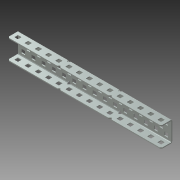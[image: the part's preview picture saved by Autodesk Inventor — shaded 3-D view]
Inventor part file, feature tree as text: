
AUTODESK INVENTOR PART (.ipt)
format: ipt  version: 2015 (Build 190159000, 159)  size: 1,670,656 bytes
history: native  units: mm (DEFAULTED — no unit token found)
features: other x74, extrude x74, pattern_linear x3, sketch x2, imported_body x1, plane x1, mirror x1
ambient origin geometry x8: Origin, YZ Plane, XZ Plane, XY Plane, X Axis, Y Axis, Z Axis, Center Point
bodies: Solid1 (feature_tree)
feature tree (156):
  imported_body  "Base1"
  sketch  "Sketch1"  dims[d1=1.1684mm]
  pattern_linear  "Rectangular Pattern1"  Spacing1=1.1684mm  [1 undecoded]
  pattern_linear  "Rectangular Pattern2"  Spacing1=0.0mm  [1 undecoded]
  pattern_linear  "Rectangular Pattern3"  Count1=15  [1 undecoded]
  plane  "Work Plane1"
  mirror  "Mirror1"
  other  "Srf1"
  other  "Srf2"
  other  "Srf3"
  other  "Srf4"
  other  "Srf5"
  other  "Srf6"
  other  "Srf17"
  other  "Srf18"
  other  "Srf19"
  other  "Srf20"
  other  "Srf21"
  other  "Srf32"
  other  "Srf33"
  other  "Srf34"
  other  "Srf7"
  other  "Srf8"
  other  "Srf9"
  other  "Srf10"
  other  "Srf11"
  other  "Srf12"
  other  "Srf13"
  other  "Srf14"
  other  "Srf15"
  other  "Srf16"
  other  "Srf22"
  other  "Srf23"
  other  "Srf24"
  other  "Srf25"
  other  "Srf26"
  other  "Srf27"
  other  "Srf28"
  other  "Srf29"
  other  "Srf30"
  other  "Srf31"
  other  "Srf35"
  other  "Srf36"
  other  "Srf37"
  other  "Srf38"
  other  "Srf39"
  other  "Srf40"
  other  "Srf41"
  other  "Srf42"
  other  "Srf43"
  other  "Srf44"
  sketch  "Sketch2"  dims[d2=0.0mm d3=1.1684mm d4=0.0mm d5=150.0mm d7=12.7mm d8=20.0mm d10=12.7mm d11=140.0mm d13=12.7mm d14=1.1684mm d15=0.0mm d16=150.0mm d18=12.7mm d19=0.0mm d20=0.0mm d21=0.0mm d22=0.0mm d23=0.0mm d24=0.0mm d25=0.0mm d26=0.0mm d27=0.0mm d28=0.0mm d29=0.0mm d30=0.0mm d31=0.0mm d32=0.0mm d33=0.0mm d34=0.0mm d35=0.0mm d36=0.0mm d37=0.0mm d38=0.0mm d39=0.0mm d40=0.0mm d41=0.0mm d42=0.0mm d43=0.0mm d44=0.0mm d45=0.0mm d46=0.0mm d47=0.0mm d48=0.0mm d49=0.0mm d50=0.0mm d51=0.0mm d52=0.0mm d53=0.0mm d54=0.0mm d55=0.0mm d56=0.0mm d57=0.0mm d58=0.0mm d59=0.0mm d60=0.0mm d61=0.0mm d62=0.0mm d63=0.0mm d64=0.0mm d65=0.0mm d66=0.0mm d67=0.0mm d68=0.0mm d69=0.0mm d70=0.0mm d71=0.0mm d72=0.0mm d73=0.0mm d74=0.0mm d75=0.0mm d76=0.0mm d77=0.0mm d78=0.0mm d79=0.0mm d80=0.0mm d81=0.0mm d82=0.0mm d83=0.0mm d84=0.0mm d85=0.0mm d86=0.0mm d87=0.0mm d88=0.0mm d89=0.0mm d90=0.0mm d91=0.0mm d92=0.0mm d93=0.0mm d94=0.0mm d95=0.0mm d96=0.0mm d97=0.0mm d98=0.0mm d99=0.0mm d100=0.0mm d101=0.0mm d102=0.0mm d103=0.0mm d104=0.0mm d105=0.0mm d106=0.0mm d107=0.0mm d108=0.0mm d109=0.0mm d110=0.0mm d111=0.0mm d112=0.0mm d113=0.0mm d114=0.0mm d115=0.0mm d116=0.0mm d117=0.0mm d118=0.0mm d119=0.0mm d120=0.0mm d121=0.0mm d122=0.0mm d123=0.0mm d124=0.0mm d125=0.0mm d126=0.0mm d127=0.0mm d128=0.0mm d129=0.0mm d130=0.0mm d131=0.0mm d132=0.0mm d133=0.0mm d134=0.0mm d135=0.0mm d136=0.0mm d137=0.0mm d138=0.0mm d139=0.0mm d140=0.0mm d141=0.0mm d142=0.0mm d143=0.0mm d144=0.0mm d145=0.0mm d146=0.0mm d147=0.0mm d148=0.0mm d149=0.0mm d150=0.0mm d151=0.0mm d152=0.0mm d153=0.0mm d154=0.0mm d155=0.0mm d156=0.0mm d157=0.0mm d158=0.0mm d159=0.0mm d160=0.0mm d161=0.0mm d162=0.0mm d163=0.0mm d164=0.0mm d165=0.0mm d166=0.0mm]
  other  "Srf45"
  other  "Srf46"
  other  "Srf47"
  other  "Srf48"
  other  "Srf49"
  other  "Srf50"
  other  "Srf51"
  other  "Srf52"
  other  "Srf53"
  other  "Srf54"
  other  "Srf55"
  other  "Srf56"
  other  "Srf57"
  other  "Srf58"
  other  "Srf59"
  other  "Srf60"
  other  "Srf61"
  other  "Srf62"
  other  "Srf63"
  other  "Srf64"
  other  "Srf65"
  other  "Srf66"
  other  "Srf67"
  other  "Srf68"
  other  "Srf69"
  other  "Srf70"
  other  "Srf71"
  other  "Srf72"
  other  "Srf73"
  other  "Srf74"
  extrude  "ExtrusionSrf1"  Depth=12.7mm
  extrude  "ExtrusionSrf2"  Depth=20.0mm
  extrude  "ExtrusionSrf45"  Depth=140.0mm
  extrude  "ExtrusionSrf3"  Depth=12.7mm
  extrude  "ExtrusionSrf4"  Depth=1.1684mm
  extrude  "ExtrusionSrf5"  TaperAngle=0.0deg  [1 undecoded]
  extrude  "ExtrusionSrf6"  Depth=150.0mm
  extrude  "ExtrusionSrf7"  Depth=12.7mm
  extrude  "ExtrusionSrf8"  TaperAngle=0.0deg  [1 undecoded]
  extrude  "ExtrusionSrf9"  TaperAngle=0.0deg  [1 undecoded]
  extrude  "ExtrusionSrf10"  TaperAngle=0.0deg  [1 undecoded]
  extrude  "ExtrusionSrf11"  TaperAngle=0.0deg  [1 undecoded]
  extrude  "ExtrusionSrf12"  TaperAngle=0.0deg  [1 undecoded]
  extrude  "ExtrusionSrf13"  TaperAngle=0.0deg  [1 undecoded]
  extrude  "ExtrusionSrf14"  TaperAngle=0.0deg  [1 undecoded]
  extrude  "ExtrusionSrf15"  TaperAngle=0.0deg  [1 undecoded]
  extrude  "ExtrusionSrf16"  TaperAngle=0.0deg  [1 undecoded]
  extrude  "ExtrusionSrf17"  TaperAngle=0.0deg  [1 undecoded]
  extrude  "ExtrusionSrf18"  TaperAngle=0.0deg  [1 undecoded]
  extrude  "ExtrusionSrf19"  TaperAngle=0.0deg  [1 undecoded]
  extrude  "ExtrusionSrf20"  TaperAngle=0.0deg  [1 undecoded]
  extrude  "ExtrusionSrf21"  TaperAngle=0.0deg  [1 undecoded]
  extrude  "ExtrusionSrf22"  TaperAngle=0.0deg  [1 undecoded]
  extrude  "ExtrusionSrf23"  TaperAngle=0.0deg  [1 undecoded]
  extrude  "ExtrusionSrf24"  TaperAngle=0.0deg  [1 undecoded]
  extrude  "ExtrusionSrf25"  TaperAngle=0.0deg  [1 undecoded]
  extrude  "ExtrusionSrf26"  TaperAngle=0.0deg  [1 undecoded]
  extrude  "ExtrusionSrf27"  TaperAngle=0.0deg  [1 undecoded]
  extrude  "ExtrusionSrf28"  TaperAngle=0.0deg  [1 undecoded]
  extrude  "ExtrusionSrf29"  TaperAngle=0.0deg  [1 undecoded]
  extrude  "ExtrusionSrf30"  TaperAngle=0.0deg  [1 undecoded]
  extrude  "ExtrusionSrf31"  TaperAngle=0.0deg  [1 undecoded]
  extrude  "ExtrusionSrf32"  TaperAngle=0.0deg  [1 undecoded]
  extrude  "ExtrusionSrf33"  TaperAngle=0.0deg  [1 undecoded]
  extrude  "ExtrusionSrf34"  TaperAngle=0.0deg  [1 undecoded]
  extrude  "ExtrusionSrf35"  TaperAngle=0.0deg  [1 undecoded]
  extrude  "ExtrusionSrf36"  TaperAngle=0.0deg  [1 undecoded]
  extrude  "ExtrusionSrf37"  TaperAngle=0.0deg  [1 undecoded]
  extrude  "ExtrusionSrf38"  TaperAngle=0.0deg  [1 undecoded]
  extrude  "ExtrusionSrf39"  TaperAngle=0.0deg  [1 undecoded]
  extrude  "ExtrusionSrf40"  TaperAngle=0.0deg  [1 undecoded]
  extrude  "ExtrusionSrf41"  TaperAngle=0.0deg  [1 undecoded]
  extrude  "ExtrusionSrf42"  TaperAngle=0.0deg  [1 undecoded]
  extrude  "ExtrusionSrf43"  TaperAngle=0.0deg  [1 undecoded]
  extrude  "ExtrusionSrf44"  TaperAngle=0.0deg  [1 undecoded]
  extrude  "ExtrusionSrf46"  TaperAngle=0.0deg  [1 undecoded]
  extrude  "ExtrusionSrf47"  TaperAngle=0.0deg  [1 undecoded]
  extrude  "ExtrusionSrf48"  TaperAngle=0.0deg  [1 undecoded]
  extrude  "ExtrusionSrf49"  TaperAngle=0.0deg  [1 undecoded]
  extrude  "ExtrusionSrf50"  TaperAngle=0.0deg  [1 undecoded]
  extrude  "ExtrusionSrf51"  TaperAngle=0.0deg  [1 undecoded]
  extrude  "ExtrusionSrf52"  TaperAngle=0.0deg  [1 undecoded]
  extrude  "ExtrusionSrf53"  TaperAngle=0.0deg  [1 undecoded]
  extrude  "ExtrusionSrf54"  TaperAngle=0.0deg  [1 undecoded]
  extrude  "ExtrusionSrf55"  TaperAngle=0.0deg  [1 undecoded]
  extrude  "ExtrusionSrf56"  TaperAngle=0.0deg  [1 undecoded]
  extrude  "ExtrusionSrf57"  TaperAngle=0.0deg  [1 undecoded]
  extrude  "ExtrusionSrf58"  TaperAngle=0.0deg  [1 undecoded]
  extrude  "ExtrusionSrf59"  TaperAngle=0.0deg  [1 undecoded]
  extrude  "ExtrusionSrf60"  TaperAngle=0.0deg  [1 undecoded]
  extrude  "ExtrusionSrf61"  TaperAngle=0.0deg  [1 undecoded]
  extrude  "ExtrusionSrf62"  TaperAngle=0.0deg  [1 undecoded]
  extrude  "ExtrusionSrf63"  TaperAngle=0.0deg  [1 undecoded]
  extrude  "ExtrusionSrf64"  TaperAngle=0.0deg  [1 undecoded]
  extrude  "ExtrusionSrf65"  TaperAngle=0.0deg  [1 undecoded]
  extrude  "ExtrusionSrf66"  TaperAngle=0.0deg  [1 undecoded]
  extrude  "ExtrusionSrf67"  TaperAngle=0.0deg  [1 undecoded]
  extrude  "ExtrusionSrf68"  TaperAngle=0.0deg  [1 undecoded]
  extrude  "ExtrusionSrf69"  TaperAngle=0.0deg  [1 undecoded]
  extrude  "ExtrusionSrf70"  TaperAngle=0.0deg  [1 undecoded]
  extrude  "ExtrusionSrf71"  TaperAngle=0.0deg  [1 undecoded]
  extrude  "ExtrusionSrf72"  TaperAngle=0.0deg  [1 undecoded]
  extrude  "ExtrusionSrf73"  TaperAngle=0.0deg  [1 undecoded]
  extrude  "ExtrusionSrf74"  TaperAngle=0.0deg  [1 undecoded]
note: 70 required parameter values undecoded (feature->parameter linkage not recoverable at this tier; creation-order binding heuristic only, values carry confidence <= 0.55)
